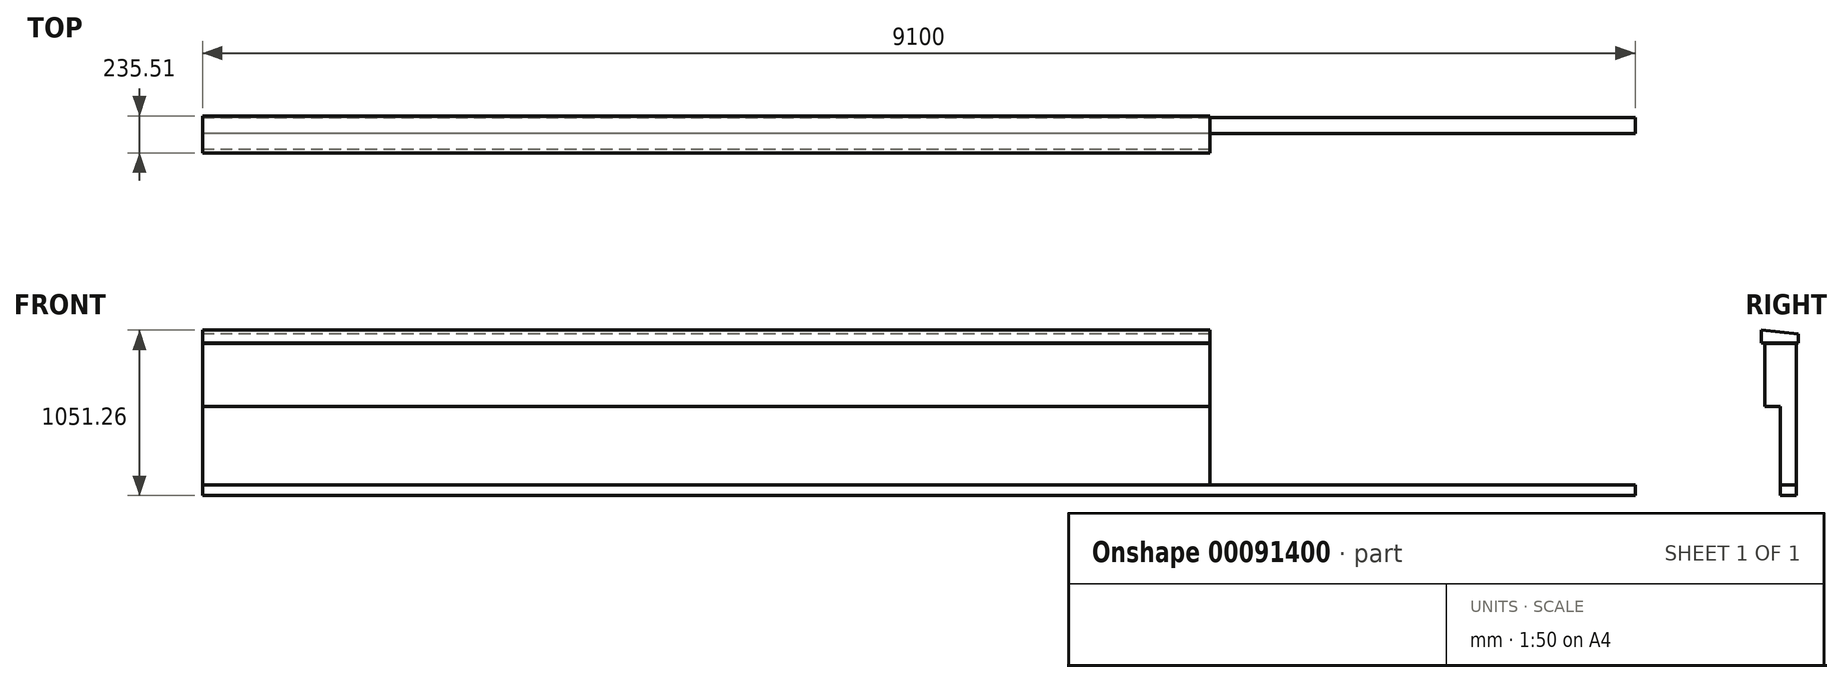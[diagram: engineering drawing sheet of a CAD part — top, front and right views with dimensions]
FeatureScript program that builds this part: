
annotation { "Feature Type Name" : "Feature", "Feature Type Description" : "" }
export const myFeature = defineFeature(function(context is Context, id is Id, definition is map)
    precondition{}
    {
        {
            var Q0;
            Q0=qCreatedBy(makeId("Right.planeOp"),FACE);
            var sketch = newSketch(context, id + "F0", { "sketchPlane" : qUnion([Q0])});
            skLineSegment(sketch, "E0.top", {"start": v(-100, -294.93) * mm, "end": v(0, -294.93) * mm});
            skLineSegment(sketch, "E0.left", {"start": v(-100, 105.07) * mm, "end": v(-100, -294.93) * mm});
            skLineSegment(sketch, "E0.right", {"start": v(100, 105.07) * mm, "end": v(100, -294.93) * mm});
            skLineSegment(sketch, "E1.left", {"start": v(100, -294.93) * mm, "end": v(100, -794.93) * mm});
            skLineSegment(sketch, "E1.right", {"start": v(0, -294.93) * mm, "end": v(0, -794.93) * mm});
            skLineSegment(sketch, "E2", {"start": v(-100, 105.07) * mm, "end": v(100, 105.07) * mm});
            skLineSegment(sketch, "E3", {"start": v(0, -794.93) * mm, "end": v(100, -794.93) * mm});
            skSolve(sketch);
        }
        {
            var Q0;
            Q0=qCreatedBy(makeId("Right.planeOp"),FACE);
            var sketch = newSketch(context, id + "F1", { "sketchPlane" : qUnion([Q0])});
            skLineSegment(sketch, "E4.bottom", {"start": v(-123.03, 107.28) * mm, "end": v(112.48, 107.28) * mm});
            skLineSegment(sketch, "E4.left", {"start": v(-123.03, 107.28) * mm, "end": v(-123.03, 190.08) * mm});
            skLineSegment(sketch, "E4.right", {"start": v(112.48, 107.28) * mm, "end": v(112.48, 163.95) * mm});
            skLineSegment(sketch, "E5", {"start": v(-123.03, 190.08) * mm, "end": v(112.48, 163.95) * mm});
            skSolve(sketch);
        }
        {
            var Q0;
            Q0=qCreatedBy(makeId("Right.planeOp"),FACE);
            var sketch = newSketch(context, id + "F2", { "sketchPlane" : qUnion([Q0])});
            skLineSegment(sketch, "E6.bottom", {"start": v(0, -794.51) * mm, "end": v(100.72, -794.51) * mm});
            skLineSegment(sketch, "E6.top", {"start": v(0, -861.18) * mm, "end": v(100.72, -861.18) * mm});
            skLineSegment(sketch, "E6.left", {"start": v(0, -794.51) * mm, "end": v(0, -861.18) * mm});
            skLineSegment(sketch, "E6.right", {"start": v(100.72, -794.51) * mm, "end": v(100.72, -861.18) * mm});
            skSolve(sketch);
        }
        {
            var Q0;
            Q0 = qSketchRegion(id + "F0", true);
            extrude(context, id + "F3", {"entities" : qUnion([Q0]), "depth" : 6400 * mm});
        }
        {
            var Q0;
            Q0 = qSketchRegion(id + "F1", true);
            extrude(context, id + "F4", {"entities" : qUnion([Q0]), "depth" : 6400 * mm});
        }
        {
            var Q0;
            Q0 = qSketchRegion(id + "F2", true);
            extrude(context, id + "F5", {"entities" : qUnion([Q0]), "depth" : 9100 * mm});
        }
    });
